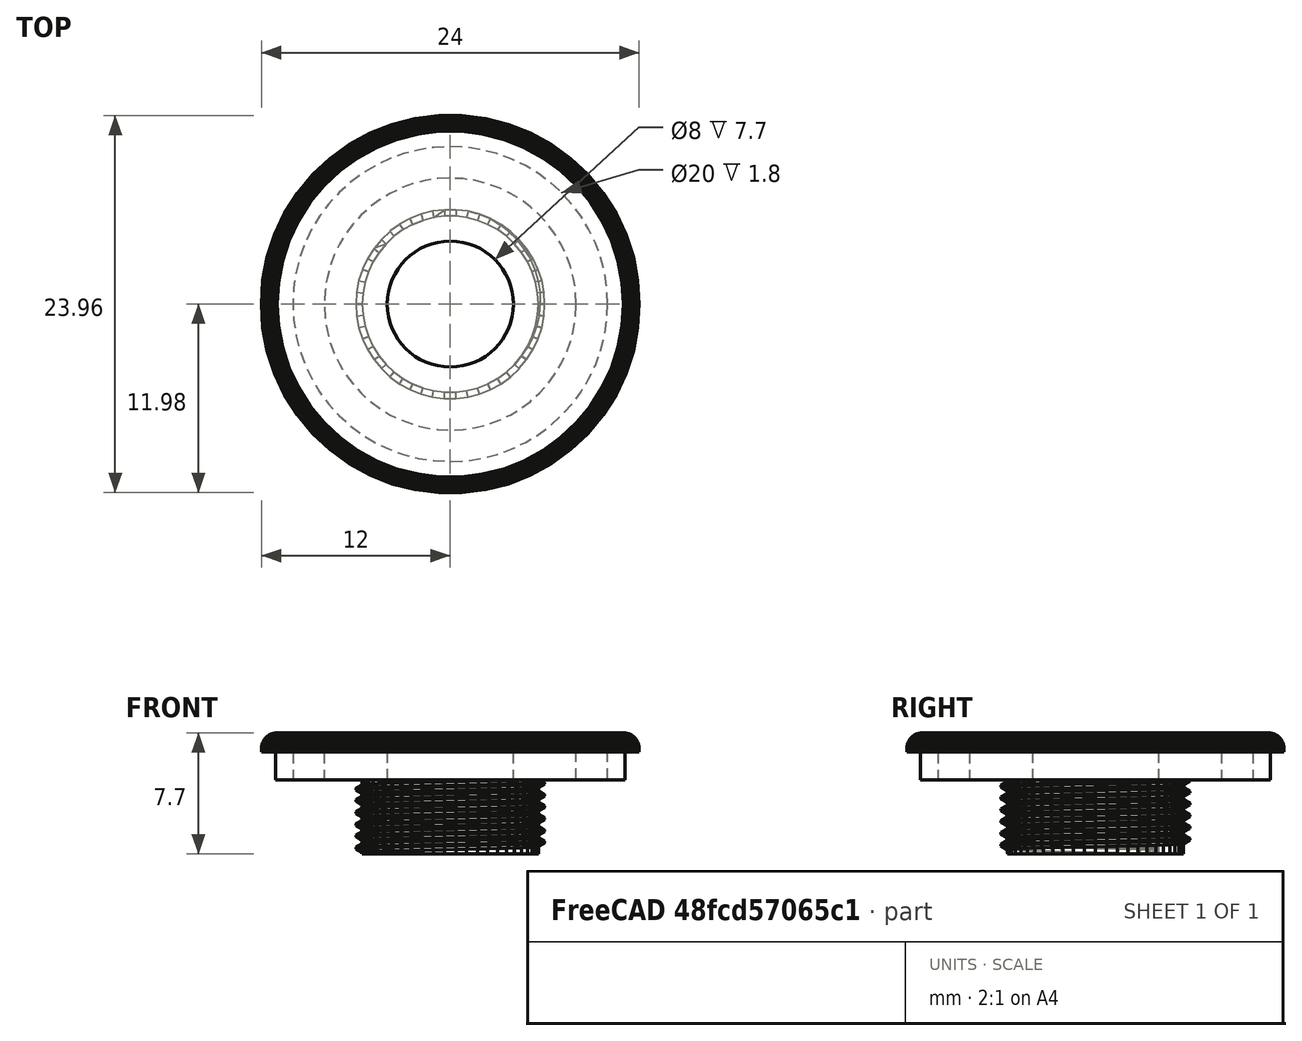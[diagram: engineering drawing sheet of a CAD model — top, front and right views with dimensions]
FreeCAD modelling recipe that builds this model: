
FCSTD DOCUMENT  (FreeCAD 1.0R38806 (Git))
Label: led-ring-encoder-washer
License: All rights reserved
LicenseURL: https://en.wikipedia.org/wiki/All_rights_reserved
objects: Part::Cylinder×5, Part::Cut×3, Part::Feature×2, Part::Fuse×1, Part::MultiFuse×1
note: 12 computed .brp shape members not serialized (recipe doc carries the construction recipe); baked Part::Feature solids carry a one-line shape summary decoded from their .brp

FEATURE [Part::Feature] polyhedron
  Placement = pos=(0,0,-0.3) rot=(0,0,1;0rad)
  shape: bbox 24 x 23.95 x 3 mm, 1228 faces (baked)
FEATURE [Part::Feature] polyhedron001
  Placement = pos=(0,0,-4) rot=(0,0,1;0rad)
  shape: bbox 12 x 11.98 x 5 mm, 1818 faces (baked)
FEATURE [Part::Fuse] union
  Base = -> polyhedron
  Refine = true
  Tool = -> polyhedron001
FEATURE [Part::Cylinder] cylinder
  Angle = 360
  AttacherType = Attacher::AttachEngine3D
  FirstAngle = 0
  Height = 20
  Placement = pos=(0,0,-10) rot=(0,0,1;0rad)
  Radius = 4
  SecondAngle = 0
FEATURE [Part::Cylinder] cylinder001
  Angle = 360
  AttacherType = Attacher::AttachEngine3D
  FirstAngle = 0
  Height = 4
  Placement = pos=(0,0,-2) rot=(0,0,1;0rad)
  Radius = 12.5
  SecondAngle = 0
FEATURE [Part::Cylinder] cylinder002
  Angle = 360
  AttacherType = Attacher::AttachEngine3D
  FirstAngle = 0
  Height = 4.05
  Placement = pos=(0,0,-2.025) rot=(0,0,1;0rad)
  Radius = 11.1
  SecondAngle = 0
FEATURE [Part::Cut] difference
  Base = -> cylinder001
  Placement = pos=(0,0,-2) rot=(0,0,1;0rad)
  Refine = true
  Tool = -> cylinder002
FEATURE [Part::Cylinder] cylinder003
  Angle = 360
  AttacherType = Attacher::AttachEngine3D
  FirstAngle = 0
  Height = 4
  Placement = pos=(0,0,-2) rot=(0,0,1;0rad)
  Radius = 10
  SecondAngle = 0
FEATURE [Part::Cylinder] cylinder004
  Angle = 360
  AttacherType = Attacher::AttachEngine3D
  FirstAngle = 0
  Height = 4.05
  Placement = pos=(0,0,-2.025) rot=(0,0,1;0rad)
  Radius = 8
  SecondAngle = 0
FEATURE [Part::Cut] difference001
  Base = -> cylinder003
  Placement = pos=(0,0,-2) rot=(0,0,1;0rad)
  Refine = true
  Tool = -> cylinder004
FEATURE [Part::MultiFuse] union001
  Refine = true
  Shapes = -> [cylinder,difference,difference001]
FEATURE [Part::Cut] difference002
  Base = -> union
  Refine = true
  Tool = -> union001
